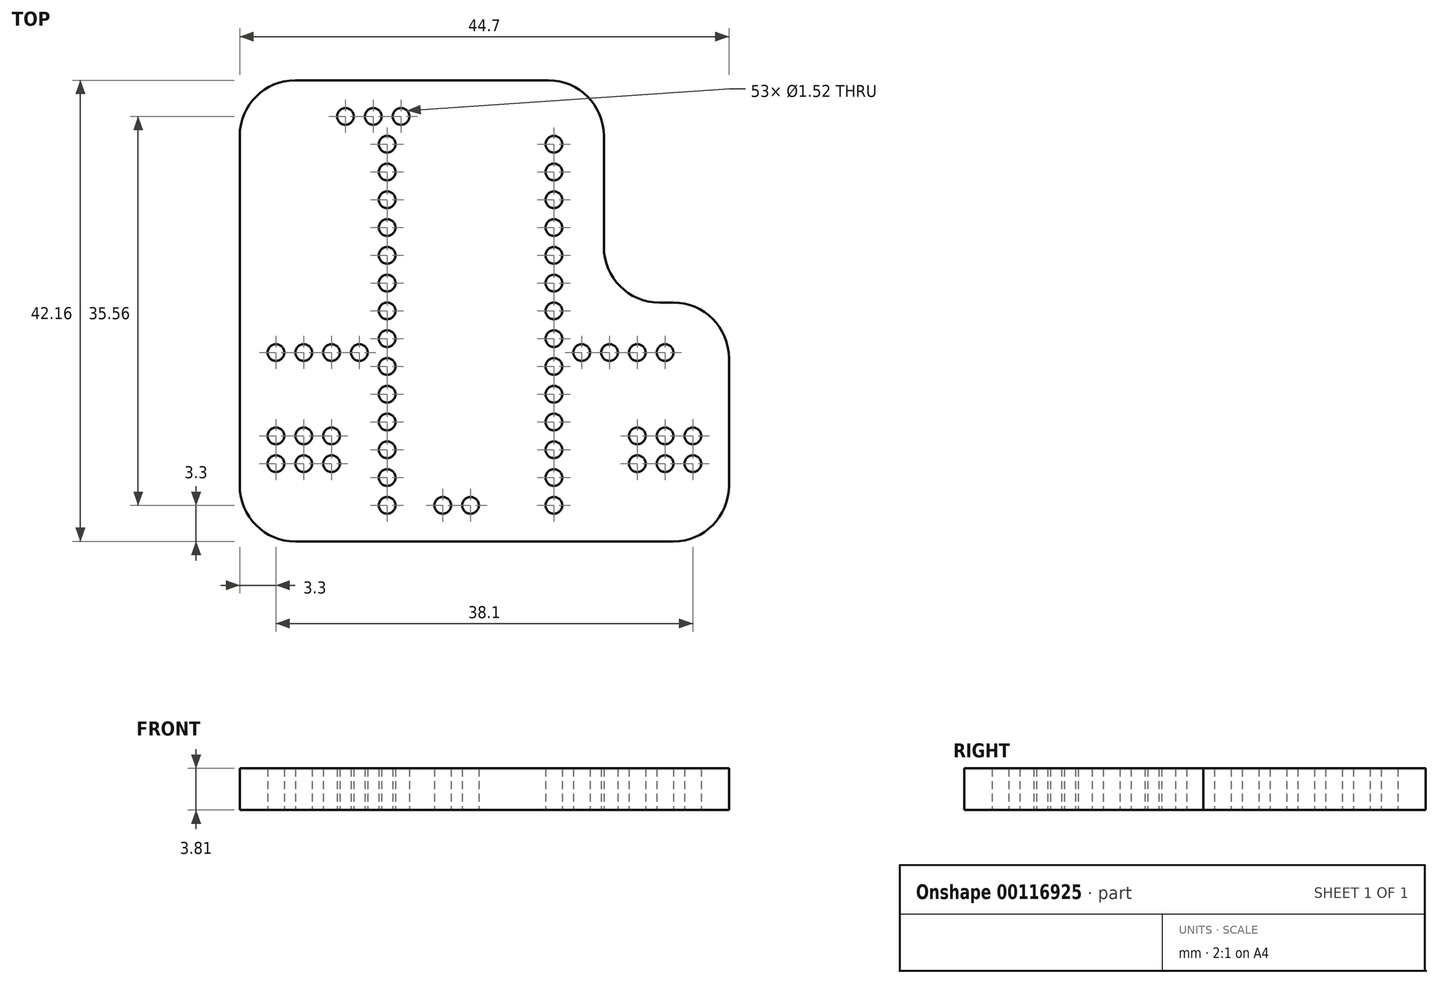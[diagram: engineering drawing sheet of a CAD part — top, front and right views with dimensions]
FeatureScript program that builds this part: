
annotation { "Feature Type Name" : "Feature", "Feature Type Description" : "" }
export const myFeature = defineFeature(function(context is Context, id is Id, definition is map)
    precondition{}
    {
        {
            var Q0;
            Q0=qCreatedBy(makeId("Top.planeOp"),FACE);
            var sketch = newSketch(context, id + "F0", { "sketchPlane" : qUnion([Q0])});
            skLineSegment(sketch, "E0.bottom", {"start": v(7.62, -16.51) * mm, "end": v(-7.62, -16.51) * mm, "construction": true});
            skLineSegment(sketch, "E0.top", {"start": v(7.62, 16.51) * mm, "end": v(-7.62, 16.51) * mm, "construction": true});
            skLineSegment(sketch, "E0.left", {"start": v(7.62, -16.51) * mm, "end": v(7.62, 16.51) * mm, "construction": true});
            skLineSegment(sketch, "E0.right", {"start": v(-7.62, -16.51) * mm, "end": v(-7.62, 16.51) * mm, "construction": true});
            skPoint(sketch, "E0.middle", {"position": v(0, 0) * mm});
            skCircle(sketch, "E1", {"center": v(-7.62, -16.51) * mm, "radius": 0.76 * mm});
            skCircle(sketch, "E2.0.1.0", {"center": v(-7.62, -13.97) * mm, "radius": 0.76 * mm});
            skCircle(sketch, "E2.0.2.0", {"center": v(-7.62, -11.43) * mm, "radius": 0.76 * mm});
            skCircle(sketch, "E2.0.3.0", {"center": v(-7.62, -8.9) * mm, "radius": 0.76 * mm});
            skCircle(sketch, "E2.0.4.0", {"center": v(-7.62, -6.35) * mm, "radius": 0.76 * mm});
            skCircle(sketch, "E2.0.5.0", {"center": v(-7.62, -3.81) * mm, "radius": 0.76 * mm});
            skCircle(sketch, "E2.0.6.0", {"center": v(-7.62, -1.27) * mm, "radius": 0.76 * mm});
            skCircle(sketch, "E2.0.7.0", {"center": v(-7.62, 1.27) * mm, "radius": 0.76 * mm});
            skCircle(sketch, "E2.0.8.0", {"center": v(-7.62, 3.81) * mm, "radius": 0.76 * mm});
            skCircle(sketch, "E2.0.9.0", {"center": v(-7.62, 6.35) * mm, "radius": 0.76 * mm});
            skCircle(sketch, "E2.0.10.0", {"center": v(-7.62, 8.9) * mm, "radius": 0.76 * mm});
            skCircle(sketch, "E2.0.11.0", {"center": v(-7.62, 11.43) * mm, "radius": 0.76 * mm});
            skCircle(sketch, "E2.0.12.0", {"center": v(-7.62, 13.97) * mm, "radius": 0.76 * mm});
            skCircle(sketch, "E2.0.13.0", {"center": v(-7.62, 16.51) * mm, "radius": 0.76 * mm});
            skCircle(sketch, "E2.1.0.0", {"center": v(7.62, -16.51) * mm, "radius": 0.76 * mm});
            skCircle(sketch, "E2.1.1.0", {"center": v(7.62, -13.97) * mm, "radius": 0.76 * mm});
            skCircle(sketch, "E2.1.2.0", {"center": v(7.62, -11.43) * mm, "radius": 0.76 * mm});
            skCircle(sketch, "E2.1.3.0", {"center": v(7.62, -8.9) * mm, "radius": 0.76 * mm});
            skCircle(sketch, "E2.1.4.0", {"center": v(7.62, -6.35) * mm, "radius": 0.76 * mm});
            skCircle(sketch, "E2.1.5.0", {"center": v(7.62, -3.81) * mm, "radius": 0.76 * mm});
            skCircle(sketch, "E2.1.6.0", {"center": v(7.62, -1.27) * mm, "radius": 0.76 * mm});
            skCircle(sketch, "E2.1.7.0", {"center": v(7.62, 1.27) * mm, "radius": 0.76 * mm});
            skCircle(sketch, "E2.1.8.0", {"center": v(7.62, 3.81) * mm, "radius": 0.76 * mm});
            skCircle(sketch, "E2.1.9.0", {"center": v(7.62, 6.35) * mm, "radius": 0.76 * mm});
            skCircle(sketch, "E2.1.10.0", {"center": v(7.62, 8.9) * mm, "radius": 0.76 * mm});
            skCircle(sketch, "E2.1.11.0", {"center": v(7.62, 11.43) * mm, "radius": 0.76 * mm});
            skCircle(sketch, "E2.1.12.0", {"center": v(7.62, 13.97) * mm, "radius": 0.76 * mm});
            skCircle(sketch, "E2.1.13.0", {"center": v(7.62, 16.51) * mm, "radius": 0.76 * mm});
            skLineSegment(sketch, "E2.direction1", {"start": v(-7.62, -16.51) * mm, "end": v(7.62, -16.51) * mm, "construction": true});
            skLineSegment(sketch, "E2.direction2", {"start": v(-7.62, -16.51) * mm, "end": v(-7.62, -13.97) * mm, "construction": true});
            skCircle(sketch, "E3", {"center": v(-11.43, 19.05) * mm, "radius": 0.76 * mm});
            skCircle(sketch, "E4.1.0.0", {"center": v(-8.9, 19.05) * mm, "radius": 0.76 * mm});
            skCircle(sketch, "E4.2.0.0", {"center": v(-6.35, 19.05) * mm, "radius": 0.76 * mm});
            skLineSegment(sketch, "E4.direction1", {"start": v(-11.43, 19.05) * mm, "end": v(-8.9, 19.05) * mm, "construction": true});
            skCircle(sketch, "E5", {"center": v(-12.7, -12.7) * mm, "radius": 0.76 * mm});
            skCircle(sketch, "E6.0.1.0", {"center": v(-12.7, -10.16) * mm, "radius": 0.76 * mm});
            skCircle(sketch, "E6.1.0.0", {"center": v(-15.24, -12.7) * mm, "radius": 0.76 * mm});
            skCircle(sketch, "E6.1.1.0", {"center": v(-15.24, -10.16) * mm, "radius": 0.76 * mm});
            skCircle(sketch, "E6.2.0.0", {"center": v(-17.78, -12.7) * mm, "radius": 0.76 * mm});
            skCircle(sketch, "E6.2.1.0", {"center": v(-17.78, -10.16) * mm, "radius": 0.76 * mm});
            skLineSegment(sketch, "E6.direction1", {"start": v(-12.7, -12.7) * mm, "end": v(-15.24, -12.7) * mm, "construction": true});
            skLineSegment(sketch, "E6.direction2", {"start": v(-12.7, -12.7) * mm, "end": v(-12.7, -10.16) * mm, "construction": true});
            skCircle(sketch, "E7", {"center": v(15.24, -12.7) * mm, "radius": 0.76 * mm});
            skLineSegment(sketch, "E8", {"start": v(-12.7, -12.7) * mm, "end": v(15.24, -12.7) * mm, "construction": true});
            skLineSegment(sketch, "E9", {"start": v(1.27, -12.7) * mm, "end": v(1.27, -6.57) * mm, "construction": true});
            skCircle(sketch, "E10.MirrorC", {"center": v(15.24, -10.16) * mm, "radius": 0.76 * mm});
            skCircle(sketch, "E11.MirrorC", {"center": v(17.78, -12.7) * mm, "radius": 0.76 * mm});
            skCircle(sketch, "E12.MirrorC", {"center": v(17.78, -10.16) * mm, "radius": 0.76 * mm});
            skCircle(sketch, "E13.MirrorC", {"center": v(20.32, -10.16) * mm, "radius": 0.76 * mm});
            skCircle(sketch, "E14.MirrorC", {"center": v(20.32, -12.7) * mm, "radius": 0.76 * mm});
            skCircle(sketch, "E15", {"center": v(10.16, -2.54) * mm, "radius": 0.76 * mm});
            skCircle(sketch, "E16.1.0.0", {"center": v(12.7, -2.54) * mm, "radius": 0.76 * mm});
            skCircle(sketch, "E16.2.0.0", {"center": v(15.24, -2.54) * mm, "radius": 0.76 * mm});
            skCircle(sketch, "E16.3.0.0", {"center": v(17.78, -2.54) * mm, "radius": 0.76 * mm});
            skLineSegment(sketch, "E16.direction1", {"start": v(10.16, -2.54) * mm, "end": v(12.7, -2.54) * mm, "construction": true});
            skCircle(sketch, "E17.MirrorC", {"center": v(-10.16, -2.54) * mm, "radius": 0.76 * mm});
            skCircle(sketch, "E18.MirrorC", {"center": v(-12.7, -2.54) * mm, "radius": 0.76 * mm});
            skCircle(sketch, "E19.MirrorC", {"center": v(-15.24, -2.54) * mm, "radius": 0.76 * mm});
            skCircle(sketch, "E20.MirrorC", {"center": v(-17.78, -2.54) * mm, "radius": 0.76 * mm});
            skCircle(sketch, "E21", {"center": v(-2.54, -16.51) * mm, "radius": 0.76 * mm});
            skCircle(sketch, "E22.1.0.0", {"center": v(0, -16.51) * mm, "radius": 0.76 * mm});
            skLineSegment(sketch, "E22.direction1", {"start": v(-2.54, -16.51) * mm, "end": v(0, -16.51) * mm, "construction": true});
            skLineSegment(sketch, "E23.bottom", {"start": v(-16, 22.35) * mm, "end": v(7.11, 22.35) * mm});
            skLineSegment(sketch, "E23.top", {"start": v(-16, -19.81) * mm, "end": v(18.54, -19.81) * mm});
            skLineSegment(sketch, "E23.left", {"start": v(-21.08, 17.27) * mm, "end": v(-21.08, -14.73) * mm});
            skLineSegment(sketch, "E23.right", {"start": v(23.62, -3.05) * mm, "end": v(23.62, -14.73) * mm});
            skPoint(sketch, "E24.visualSharp", {"position": v(-21.08, 22.35) * mm});
            skArc(sketch, "E24.filletArc", {"start": v(-16, 22.35) * mm, "mid": v(-19.6, 20.86) * mm, "end": v(-21.08, 17.27) * mm});
            skPoint(sketch, "E25.visualSharp", {"position": v(23.62, 22.35) * mm});
            skPoint(sketch, "E26.visualSharp", {"position": v(23.62, -19.81) * mm});
            skArc(sketch, "E26.filletArc", {"start": v(18.54, -19.81) * mm, "mid": v(22.13, -18.32) * mm, "end": v(23.62, -14.73) * mm});
            skPoint(sketch, "E27.visualSharp", {"position": v(-21.08, -19.81) * mm});
            skArc(sketch, "E27.filletArc", {"start": v(-21.08, -14.73) * mm, "mid": v(-19.6, -18.32) * mm, "end": v(-16, -19.81) * mm});
            skLineSegment(sketch, "E28", {"start": v(12.2, 17.27) * mm, "end": v(12.2, 7.11) * mm});
            skLineSegment(sketch, "E29", {"start": v(17.27, 2.03) * mm, "end": v(18.54, 2.03) * mm});
            skPoint(sketch, "E30.visualSharp", {"position": v(12.2, 22.35) * mm});
            skArc(sketch, "E30.filletArc", {"start": v(12.2, 17.27) * mm, "mid": v(10.7, 20.86) * mm, "end": v(7.11, 22.35) * mm});
            skPoint(sketch, "E31.visualSharp", {"position": v(12.2, 2.03) * mm});
            skArc(sketch, "E31.filletArc", {"start": v(12.2, 7.11) * mm, "mid": v(13.68, 3.52) * mm, "end": v(17.27, 2.03) * mm});
            skPoint(sketch, "E32.visualSharp", {"position": v(23.62, 2.03) * mm});
            skArc(sketch, "E32.filletArc", {"start": v(23.62, -3.05) * mm, "mid": v(22.13, 0.54) * mm, "end": v(18.54, 2.03) * mm});
            skSolve(sketch);
        }
        {
            var Q0;
            Q0=makeQuery(id+"F0.imprint","IMPRINT",FACE,{"disambiguationData":[TD([[makeQuery(id+"F0.imprint","IMPRINT",EDGE,{"derivedFrom":sQuery(id+"F0.wireOp",EDGE,"E1")}),-1.0]])]});
            extrude(context, id + "F1", {"entities" : qUnion([Q0]), "depth" : 3.8 * mm, "offsetDistance" : 25.4 * mm});
        }
    });
